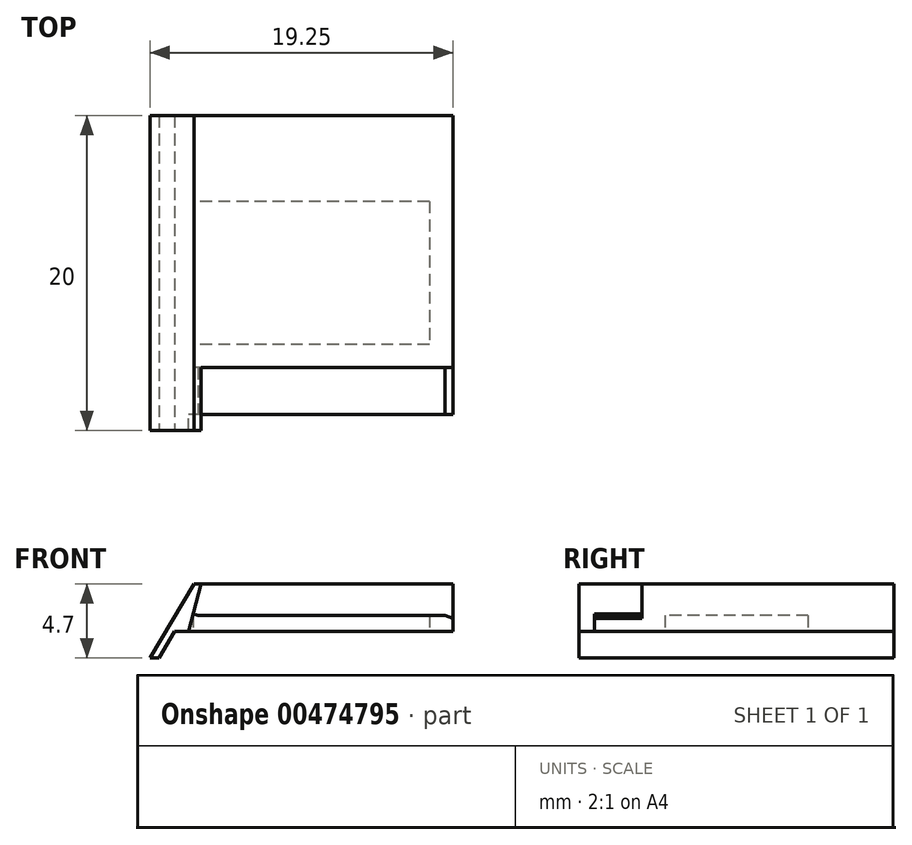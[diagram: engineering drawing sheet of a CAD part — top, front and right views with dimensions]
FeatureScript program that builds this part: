
annotation { "Feature Type Name" : "Feature", "Feature Type Description" : "" }
export const myFeature = defineFeature(function(context is Context, id is Id, definition is map)
    precondition{}
    {
        {
            var Q0;
            Q0=qCreatedBy(makeId("Front.planeOp"),FACE);
            var sketch = newSketch(context, id + "F0", { "sketchPlane" : qUnion([Q0])});
            skLineSegment(sketch, "E0", {"start": v(-19.25, -1.7) * mm, "end": v(-16.45, 3) * mm});
            skLineSegment(sketch, "E1", {"start": v(-16.45, 3) * mm, "end": v(0, 3) * mm});
            skLineSegment(sketch, "E2", {"start": v(0, 3) * mm, "end": v(0, 0) * mm});
            skLineSegment(sketch, "E3", {"start": v(0, 0) * mm, "end": v(-17.08, 0) * mm});
            skLineSegment(sketch, "E4", {"start": v(-17.08, 0) * mm, "end": v(-18.09, -1.7) * mm});
            skLineSegment(sketch, "E5", {"start": v(-18.09, -1.7) * mm, "end": v(-19.25, -1.7) * mm});
            skSolve(sketch);
        }
        {
            var Q0;
            Q0=makeQuery(id+"F0.imprint","IMPRINT",FACE,{"disambiguationData":[TD([[makeQuery(id+"F0.imprint","IMPRINT",EDGE,{"derivedFrom":sQuery(id+"F0.wireOp",EDGE,"E0")}),-1.0]])]});
            extrude(context, id + "F1", {"entities" : qUnion([Q0]), "depth" : 20 * mm});
        }
        {
            var Q0;
            Q0=makeQuery(id+"F1.opExtrude","CAP_FACE",FACE,{"disambiguationData":[OSD([sQuery(id+"F0.wireOp",EDGE,"E0"),sQuery(id+"F0.wireOp",EDGE,"E1"),sQuery(id+"F0.wireOp",EDGE,"E2"),sQuery(id+"F0.wireOp",EDGE,"E3"),sQuery(id+"F0.wireOp",EDGE,"E4"),sQuery(id+"F0.wireOp",EDGE,"E5")])],"isStart":false});
            var sketch = newSketch(context, id + "F2", { "sketchPlane" : qUnion([Q0])});
            skLineSegment(sketch, "E6", {"start": v(-0.5, 1) * mm, "end": v(0, 0.82) * mm});
            skLineSegment(sketch, "E7", {"start": v(0, 0.82) * mm, "end": v(0, 3) * mm});
            skLineSegment(sketch, "E8", {"start": v(0, 3) * mm, "end": v(-16, 3) * mm});
            skLineSegment(sketch, "E9", {"start": v(-0.5, 1) * mm, "end": v(-16.2, 1) * mm});
            skLineSegment(sketch, "E10", {"start": v(-16.2, 1) * mm, "end": v(-16.5, 1.1) * mm});
            skLineSegment(sketch, "E11", {"start": v(-16, 3) * mm, "end": v(-16.5, 1.1) * mm});
            skSolve(sketch);
        }
        {
            var Q0;
            Q0 = qSketchRegion(id + "F2", true);
            extrude(context, id + "F3", {"entities" : qUnion([Q0]), "operationType" : NewBodyOperationType.REMOVE, "oppositeDirection" : true, "depth" : 4 * mm});
        }
        {
            var Q0;
            Q0=makeQuery(id+"F1.opExtrude","CAP_FACE",FACE,{"disambiguationData":[OSD([sQuery(id+"F0.wireOp",EDGE,"E0"),sQuery(id+"F0.wireOp",EDGE,"E1"),sQuery(id+"F0.wireOp",EDGE,"E2"),sQuery(id+"F0.wireOp",EDGE,"E3"),sQuery(id+"F0.wireOp",EDGE,"E4"),sQuery(id+"F0.wireOp",EDGE,"E5")])],"isStart":false});
            var sketch = newSketch(context, id + "F4", { "sketchPlane" : qUnion([Q0])});
            skLineSegment(sketch, "E12", {"start": v(0, 0.82) * mm, "end": v(-0.5, 1) * mm});
            skLineSegment(sketch, "E13", {"start": v(-0.5, 1) * mm, "end": v(-16.2, 1) * mm});
            skLineSegment(sketch, "E14", {"start": v(-16.2, 1) * mm, "end": v(-16.5, 1.1) * mm});
            skLineSegment(sketch, "E15", {"start": v(-16.5, 1.1) * mm, "end": v(-17.06, -1) * mm});
            skLineSegment(sketch, "E16", {"start": v(-17.06, -1) * mm, "end": v(0, -1) * mm});
            skLineSegment(sketch, "E17", {"start": v(0, -1) * mm, "end": v(0, 0.82) * mm});
            skSolve(sketch);
        }
        {
            var Q0;
            Q0 = qSketchRegion(id + "F4", true);
            extrude(context, id + "F5", {"entities" : qUnion([Q0]), "operationType" : NewBodyOperationType.REMOVE, "oppositeDirection" : true, "depth" : 1 * mm});
        }
        {
            var Q0;
            Q0=makeQuery(id+"F1.opExtrude","CAP_FACE",FACE,{"disambiguationData":[OSD([sQuery(id+"F0.wireOp",EDGE,"E0"),sQuery(id+"F0.wireOp",EDGE,"E1"),sQuery(id+"F0.wireOp",EDGE,"E2"),sQuery(id+"F0.wireOp",EDGE,"E3"),sQuery(id+"F0.wireOp",EDGE,"E4"),sQuery(id+"F0.wireOp",EDGE,"E5")])],"isStart":false});
            var sketch = newSketch(context, id + "F6", { "sketchPlane" : qUnion([Q0])});
            skLineSegment(sketch, "E18", {"start": v(-18.09, -1.7) * mm, "end": v(-17.08, 0) * mm});
            skLineSegment(sketch, "E19", {"start": v(-17.08, 0) * mm, "end": v(-17.68, 0) * mm});
            skLineSegment(sketch, "E20", {"start": v(-17.68, 0) * mm, "end": v(-18.67, -1.7) * mm});
            skLineSegment(sketch, "E21", {"start": v(-18.67, -1.7) * mm, "end": v(-18.09, -1.7) * mm});
            skSolve(sketch);
        }
        {
            var Q0;
            Q0 = qSketchRegion(id + "F6", true);
            extrude(context, id + "F7", {"entities" : qUnion([Q0]), "operationType" : NewBodyOperationType.REMOVE, "endBound" : BoundingType.THROUGH_ALL, "oppositeDirection" : true, "depth" : 25 * mm});
        }
        {
            var Q0;
            Q0=makeQuery(id+"F1.opExtrude","SWEPT_FACE",FACE,{"disambiguationData":[OSD([sQuery(id+"F0.wireOp",EDGE,"E1")])]});
            var sketch = newSketch(context, id + "F8", { "sketchPlane" : qUnion([Q0])});
            skLineSegment(sketch, "E22", {"start": v(-16.45, -20) * mm, "end": v(-16.45, 0) * mm, "construction": true});
            skPoint(sketch, "E23", {"position": v(-16.45, -10) * mm});
            skLineSegment(sketch, "E24", {"start": v(-16.45, -10) * mm, "end": v(0, -10) * mm, "construction": true});
            skSolve(sketch);
        }
        {
            var Q0;
            Q0=sQuery(id+"F8.wireOp",EDGE,"E24");
            cPlane(context, id + "F9", {"entities" : qUnion([Q0]), "cplaneType" : CPlaneType.LINE_ANGLE, "offset" : 25 * mm, "angle" : 0 * degree, "width" : 150 * mm, "height" : 150 * mm});
        }
        {
            var Q0;
            Q0=makeQuery(id+"F7.boolean.opBoolean","MERGE",FACE,{"derivedFrom":[makeQuery(id+"F1.opExtrude","SWEPT_FACE",FACE,{"disambiguationData":[OSD([sQuery(id+"F0.wireOp",EDGE,"E3")])]}),makeQuery(id+"F7.opExtrude","SWEPT_FACE",FACE,{"disambiguationData":[OSD([sQuery(id+"F6.wireOp",EDGE,"E19")])]})]});
            var sketch = newSketch(context, id + "F10", { "sketchPlane" : qUnion([Q0])});
            skLineSegment(sketch, "E25.bottom", {"start": v(-1.5, 5.45) * mm, "end": v(-16.5, 5.45) * mm});
            skLineSegment(sketch, "E25.top", {"start": v(-1.5, 14.55) * mm, "end": v(-16.5, 14.55) * mm});
            skLineSegment(sketch, "E25.left", {"start": v(-1.5, 5.45) * mm, "end": v(-1.5, 14.55) * mm});
            skLineSegment(sketch, "E25.right", {"start": v(-16.5, 5.45) * mm, "end": v(-16.5, 14.55) * mm});
            skSolve(sketch);
        }
        {
            var Q0;
            Q0 = qSketchRegion(id + "F10", true);
            extrude(context, id + "F11", {"entities" : qUnion([Q0]), "operationType" : NewBodyOperationType.REMOVE, "oppositeDirection" : true, "depth" : 1 * mm});
        }
    });
